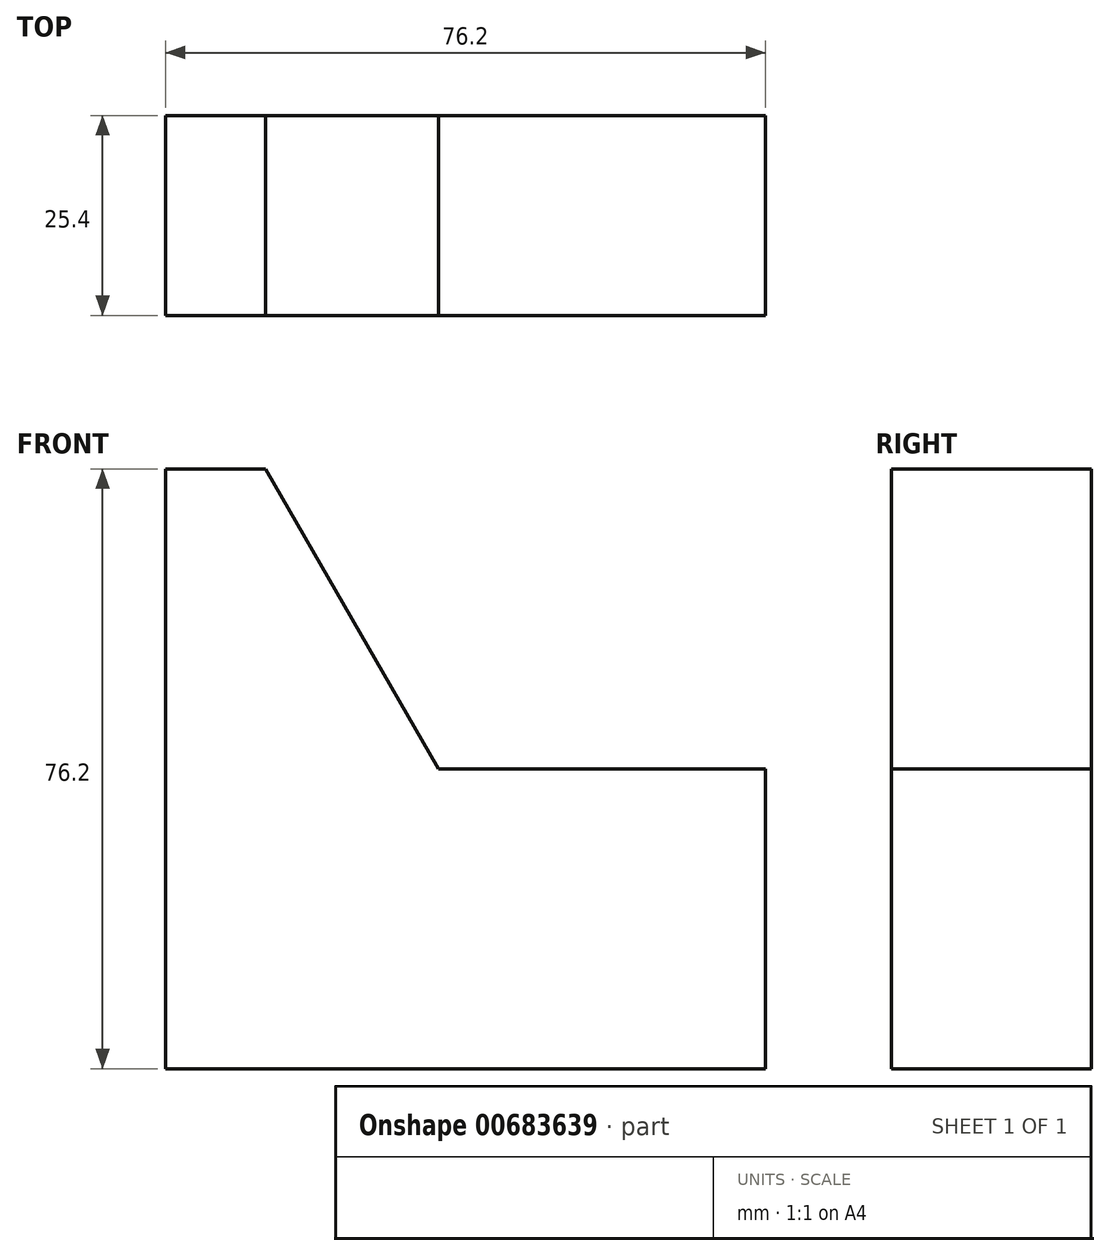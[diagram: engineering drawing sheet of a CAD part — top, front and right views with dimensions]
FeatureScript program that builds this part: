
annotation { "Feature Type Name" : "Feature", "Feature Type Description" : "" }
export const myFeature = defineFeature(function(context is Context, id is Id, definition is map)
    precondition{}
    {
        {
            var Q0;
            Q0=qCreatedBy(makeId("Front.planeOp"),FACE);
            var sketch = newSketch(context, id + "F0", { "sketchPlane" : qUnion([Q0])});
            skLineSegment(sketch, "E0", {"start": v(-88.9, 76.2) * mm, "end": v(-88.9, 0) * mm});
            skLineSegment(sketch, "E1", {"start": v(-88.9, 0) * mm, "end": v(-12.7, 0) * mm});
            skLineSegment(sketch, "E2", {"start": v(-12.7, 0) * mm, "end": v(-12.7, 38.1) * mm});
            skLineSegment(sketch, "E3", {"start": v(-12.7, 38.1) * mm, "end": v(-54.2, 38.1) * mm});
            skLineSegment(sketch, "E4", {"start": v(-54.2, 38.1) * mm, "end": v(-76.2, 76.2) * mm});
            skLineSegment(sketch, "E5", {"start": v(-76.2, 76.2) * mm, "end": v(-88.9, 76.2) * mm});
            skSolve(sketch);
        }
        {
            var Q0;
            Q0 = qSketchRegion(id + "F0", true);
            extrude(context, id + "F1", {"entities" : qUnion([Q0]), "depth" : 25.4 * mm, "offsetDistance" : 25.4 * mm});
        }
    });
